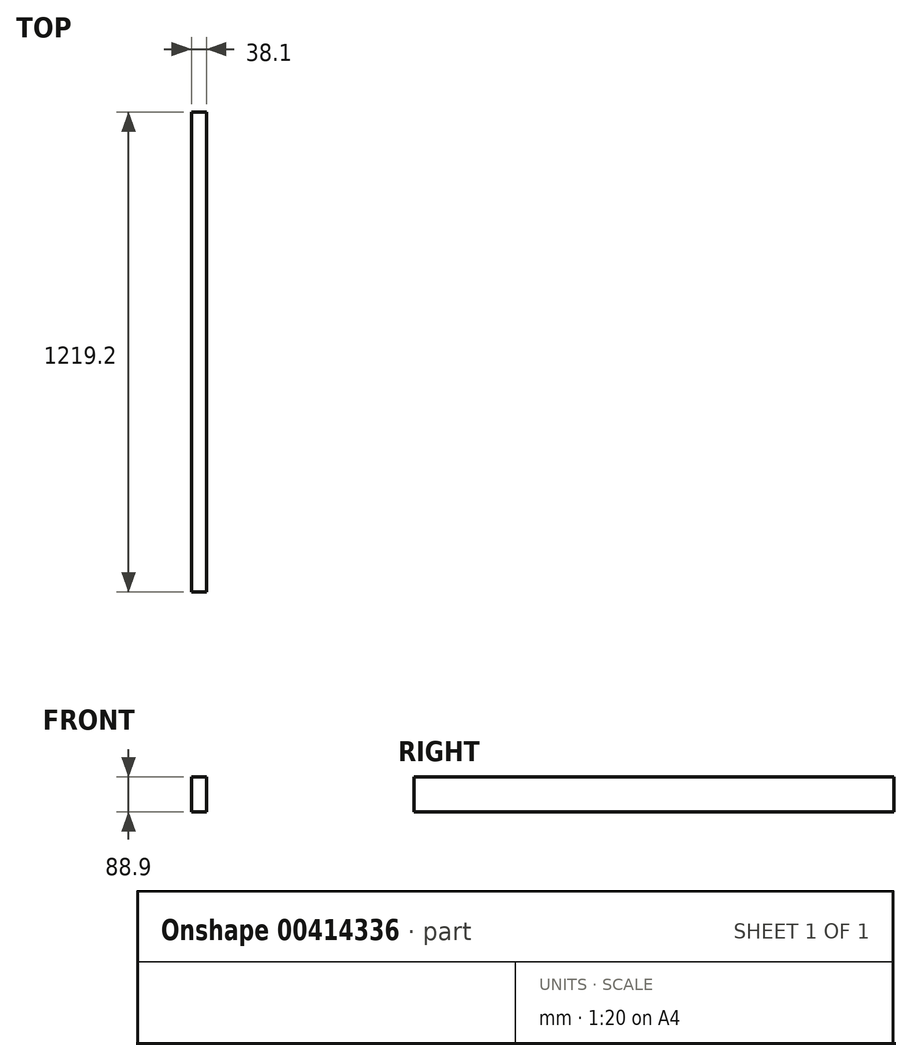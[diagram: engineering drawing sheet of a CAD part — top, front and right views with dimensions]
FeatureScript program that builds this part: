
annotation { "Feature Type Name" : "Feature", "Feature Type Description" : "" }
export const myFeature = defineFeature(function(context is Context, id is Id, definition is map)
    precondition{}
    {
        {
            var Q0;
            Q0=qCreatedBy(makeId("Top.planeOp"),FACE);
            var sketch = newSketch(context, id + "F0", { "sketchPlane" : qUnion([Q0])});
            skLineSegment(sketch, "E0.bottom", {"start": v(-19.05, 609.6) * mm, "end": v(19.05, 609.6) * mm});
            skLineSegment(sketch, "E0.top", {"start": v(-19.05, -609.6) * mm, "end": v(19.05, -609.6) * mm});
            skLineSegment(sketch, "E0.left", {"start": v(-19.05, 609.6) * mm, "end": v(-19.05, -609.6) * mm});
            skLineSegment(sketch, "E0.right", {"start": v(19.05, 609.6) * mm, "end": v(19.05, -609.6) * mm});
            skPoint(sketch, "E0.middle", {"position": v(0, 0) * mm});
            skSolve(sketch);
        }
        {
            var Q0;
            Q0 = qSketchRegion(id + "F0", true);
            extrude(context, id + "F1", {"entities" : qUnion([Q0]), "depth" : 88.9 * mm});
        }
    });
